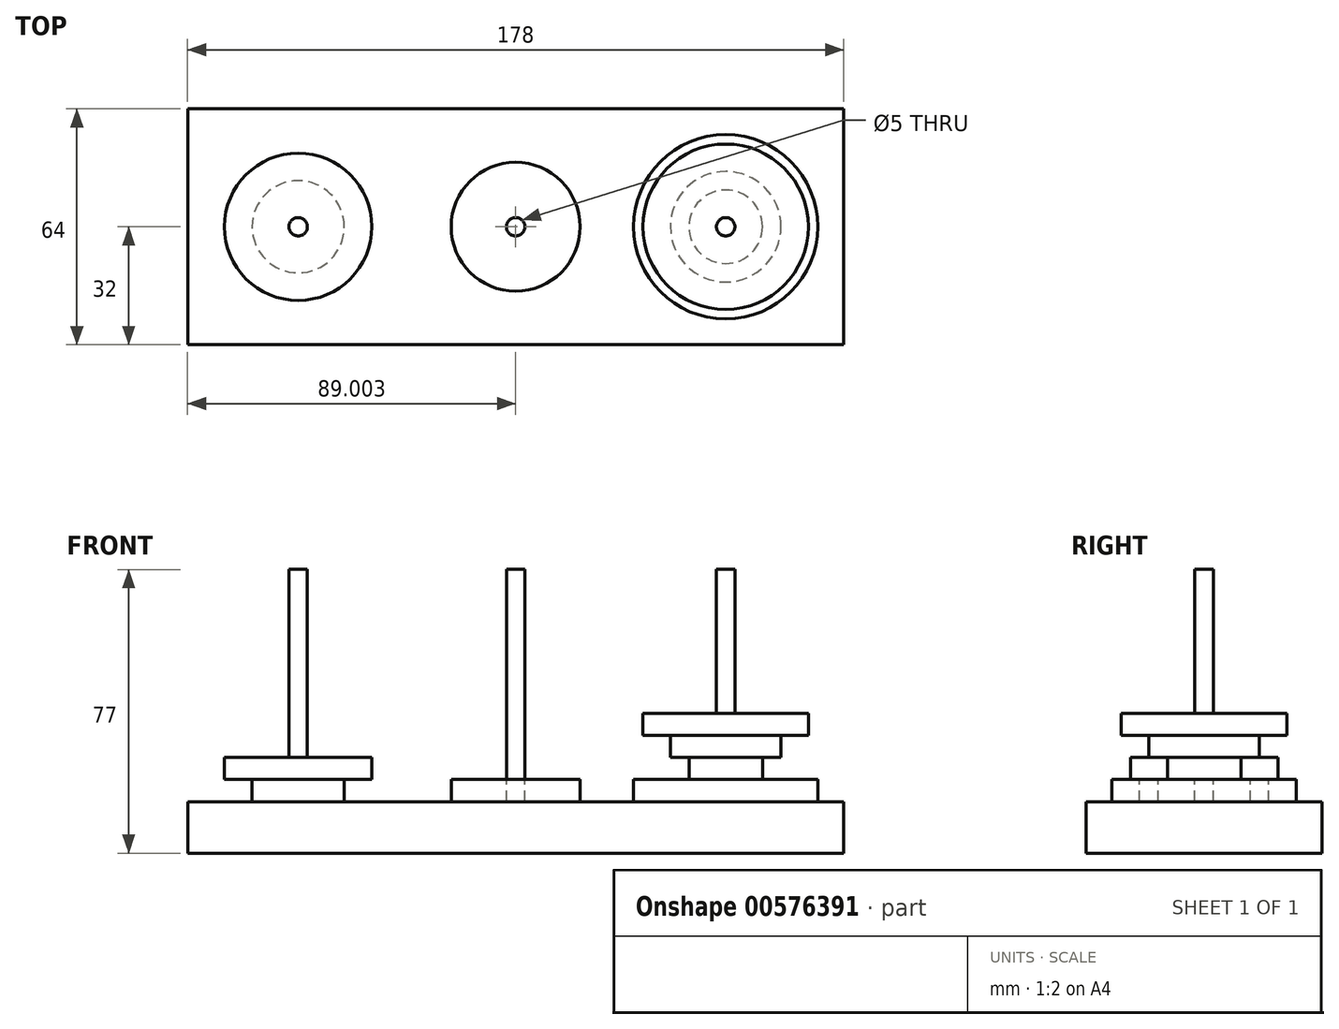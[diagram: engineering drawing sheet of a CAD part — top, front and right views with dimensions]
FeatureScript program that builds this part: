
annotation { "Feature Type Name" : "Feature", "Feature Type Description" : "" }
export const myFeature = defineFeature(function(context is Context, id is Id, definition is map)
    precondition{}
    {
        {
            var Q0;
            Q0=qCreatedBy(makeId("Front.planeOp"),FACE);
            var sketch = newSketch(context, id + "F0", { "sketchPlane" : qUnion([Q0])});
            skLineSegment(sketch, "E0", {"start": v(44.25, 49.56) * mm, "end": v(222.25, 49.56) * mm});
            skLineSegment(sketch, "E1", {"start": v(222.25, 49.56) * mm, "end": v(222.25, 63.56) * mm});
            skLineSegment(sketch, "E2", {"start": v(222.25, 63.56) * mm, "end": v(44.25, 63.56) * mm});
            skLineSegment(sketch, "E3", {"start": v(44.25, 63.56) * mm, "end": v(44.25, 49.56) * mm});
            skSolve(sketch);
        }
        {
            var Q0;
            Q0=makeQuery(id+"F0.imprint","IMPRINT",FACE,{"disambiguationData":[TD([[makeQuery(id+"F0.imprint","IMPRINT",EDGE,{"derivedFrom":sQuery(id+"F0.wireOp",EDGE,"E0")}),1.0]])]});
            extrude(context, id + "F1", {"entities" : qUnion([Q0]), "oppositeDirection" : true, "depth" : 64 * mm, "offsetDistance" : 25 * mm});
        }
        {
            var Q0;
            Q0=makeQuery(id+"F1.opExtrude","CAP_FACE",FACE,{"disambiguationData":[OSD([sQuery(id+"F0.wireOp",EDGE,"E0"),sQuery(id+"F0.wireOp",EDGE,"E1"),sQuery(id+"F0.wireOp",EDGE,"E2"),sQuery(id+"F0.wireOp",EDGE,"E3")])],"isStart":true});
            var sketch = newSketch(context, id + "F2", { "sketchPlane" : qUnion([Q0])});
            skLineSegment(sketch, "E4", {"start": v(44.25, 63.56) * mm, "end": v(103.55, 63.56) * mm});
            skLineSegment(sketch, "E5", {"start": v(103.55, 63.56) * mm, "end": v(162.85, 63.56) * mm});
            skLineSegment(sketch, "E6", {"start": v(162.85, 63.56) * mm, "end": v(222.25, 63.56) * mm});
            skSolve(sketch);
        }
        {
            var Q0;
            Q0=makeQuery(id+"F1.opExtrude","SWEPT_FACE",FACE,{"disambiguationData":[OSD([sQuery(id+"F0.wireOp",EDGE,"E2")])]});
            var sketch = newSketch(context, id + "F3", { "sketchPlane" : qUnion([Q0])});
            skCircle(sketch, "E7", {"center": v(74.25, 32) * mm, "radius": 2.5 * mm});
            skCircle(sketch, "E8", {"center": v(133.25, 32) * mm, "radius": 2.5 * mm});
            skCircle(sketch, "E9", {"center": v(190.25, 32) * mm, "radius": 2.5 * mm});
            skSolve(sketch);
        }
        {
            var Q0;
            Q0=makeQuery(id+"F3.imprint","IMPRINT",FACE,{"disambiguationData":[TD([[makeQuery(id+"F3.imprint","IMPRINT",EDGE,{"derivedFrom":sQuery(id+"F3.wireOp",EDGE,"E7")}),1.0]])]});
            var Q1;
            Q1=makeQuery(id+"F3.imprint","IMPRINT",FACE,{"disambiguationData":[TD([[makeQuery(id+"F3.imprint","IMPRINT",EDGE,{"derivedFrom":sQuery(id+"F3.wireOp",EDGE,"E8")}),1.0]])]});
            var Q2;
            Q2=makeQuery(id+"F3.imprint","IMPRINT",FACE,{"disambiguationData":[TD([[makeQuery(id+"F3.imprint","IMPRINT",EDGE,{"derivedFrom":sQuery(id+"F3.wireOp",EDGE,"E9")}),1.0]])]});
            extrude(context, id + "F4", {"entities" : qUnion([Q0, Q1, Q2]), "operationType" : NewBodyOperationType.ADD, "depth" : 63 * mm, "offsetDistance" : 25 * mm});
        }
        {
            var Q0;
            Q0=makeQuery(id+"F1.opExtrude","SWEPT_FACE",FACE,{"disambiguationData":[OSD([sQuery(id+"F0.wireOp",EDGE,"E2")])]});
            var sketch = newSketch(context, id + "F5", { "sketchPlane" : qUnion([Q0])});
            skLineSegment(sketch, "E10", {"start": v(192.75, 32) * mm, "end": v(215.25, 32) * mm});
            skPoint(sketch, "E10.startSnap0", {"position": v(222.25, 32) * mm});
            skPoint(sketch, "E10.endSnap0", {"position": v(222.25, 32) * mm});
            skSolve(sketch);
        }
        {
            var Q0;
            Q0=sQuery(id+"F5.wireOp",EDGE,"E10");
            extrude(context, id + "F6", {"bodyType" : ToolBodyType.SURFACE, "surfaceEntities" : qUnion([Q0]), "depth" : 6 * mm, "offsetDistance" : 25 * mm});
        }
        {
            var Q0;
            Q0=makeQuery(id+"F6.opExtrude","SWEPT_FACE",FACE,{"disambiguationData":[OSD([sQuery(id+"F5.wireOp",EDGE,"E10")])]});
            var Q1;
            Q1=makeQuery(id+"F4.opExtrude","SWEPT_FACE",FACE,{"disambiguationData":[OSD([sQuery(id+"F3.wireOp",EDGE,"E9")])]});
            revolve(context, id + "F7", {"operationType" : NewBodyOperationType.ADD, "entities" : qUnion([Q0]), "axis" : qUnion([Q1]), "revolveType" : RevolveType.FULL});
        }
        {
            var Q0;
            Q0=makeQuery(id+"F1.opExtrude","SWEPT_FACE",FACE,{"disambiguationData":[OSD([sQuery(id+"F0.wireOp",EDGE,"E2")])]});
            var sketch = newSketch(context, id + "F8", { "sketchPlane" : qUnion([Q0])});
            skLineSegment(sketch, "E11", {"start": v(71.75, 32) * mm, "end": v(61.75, 32) * mm});
            skPoint(sketch, "E11.startSnap0", {"position": v(44.25, 32) * mm});
            skLineSegment(sketch, "E12", {"start": v(130.75, 32) * mm, "end": v(115.75, 32) * mm});
            skSolve(sketch);
        }
        {
            var Q0;
            Q0=sQuery(id+"F8.wireOp",EDGE,"E11");
            var Q1;
            Q1=sQuery(id+"F8.wireOp",EDGE,"E12");
            extrude(context, id + "F9", {"bodyType" : ToolBodyType.SURFACE, "surfaceEntities" : qUnion([Q0, Q1]), "depth" : 6 * mm, "offsetDistance" : 25 * mm});
        }
        {
            var Q0;
            Q0=makeQuery(id+"F9.opExtrude","SWEPT_FACE",FACE,{"disambiguationData":[OSD([sQuery(id+"F8.wireOp",EDGE,"E11")])]});
            var Q1;
            Q1=makeQuery(id+"F4.opExtrude","SWEPT_FACE",FACE,{"disambiguationData":[OSD([sQuery(id+"F3.wireOp",EDGE,"E7")])]});
            revolve(context, id + "F10", {"operationType" : NewBodyOperationType.ADD, "entities" : qUnion([Q0]), "axis" : qUnion([Q1]), "revolveType" : RevolveType.FULL});
        }
        {
            var Q0;
            Q0=makeQuery(id+"F9.opExtrude","SWEPT_FACE",FACE,{"disambiguationData":[OSD([sQuery(id+"F8.wireOp",EDGE,"E12")])]});
            var Q1;
            Q1=makeQuery(id+"F4.opExtrude","SWEPT_FACE",FACE,{"disambiguationData":[OSD([sQuery(id+"F3.wireOp",EDGE,"E8")])]});
            revolve(context, id + "F11", {"entities" : qUnion([Q0]), "axis" : qUnion([Q1]), "revolveType" : RevolveType.FULL});
        }
        {
            var Q0;
            {var subQ0=sQuery(id+"F5.wireOp",EDGE,"E10");Q0=makeQuery(id+"F7.opRevolve","SWEPT_FACE",FACE,{"disambiguationData":[OSD([subQ0]),TDD([makeQuery(id+"F6.opExtrude","CAP_EDGE",EDGE,{"disambiguationData":[OSD([subQ0])],"isStart":false})])]});}
            var sketch = newSketch(context, id + "F12", { "sketchPlane" : qUnion([Q0])});
            skLineSegment(sketch, "E13", {"start": v(187.92, 32.89) * mm, "end": v(181.36, 36.53) * mm});
            skSolve(sketch);
        }
        {
            var Q0;
            Q0=sQuery(id+"F12.wireOp",EDGE,"E13");
            extrude(context, id + "F13", {"bodyType" : ToolBodyType.SURFACE, "surfaceEntities" : qUnion([Q0]), "depth" : 6 * mm, "offsetDistance" : 25 * mm});
        }
        {
            var Q0;
            Q0=makeQuery(id+"F13.opExtrude","SWEPT_FACE",FACE,{"disambiguationData":[OSD([sQuery(id+"F12.wireOp",EDGE,"E13")])]});
            var Q1;
            Q1=makeQuery(id+"F4.opExtrude","SWEPT_FACE",FACE,{"disambiguationData":[OSD([sQuery(id+"F3.wireOp",EDGE,"E9")])]});
            revolve(context, id + "F14", {"operationType" : NewBodyOperationType.ADD, "entities" : qUnion([Q0]), "axis" : qUnion([Q1]), "revolveType" : RevolveType.FULL});
        }
        {
            var Q0;
            {var subQ0=sQuery(id+"F8.wireOp",EDGE,"E11");Q0=makeQuery(id+"F10.opRevolve","SWEPT_FACE",FACE,{"disambiguationData":[OSD([subQ0]),TDD([makeQuery(id+"F9.opExtrude","CAP_EDGE",EDGE,{"disambiguationData":[OSD([subQ0])],"isStart":false})])]});}
            var sketch = newSketch(context, id + "F15", { "sketchPlane" : qUnion([Q0])});
            skLineSegment(sketch, "E14", {"start": v(76.75, 31.97) * mm, "end": v(94.25, 31.97) * mm});
            skSolve(sketch);
        }
        {
            var Q0;
            Q0=sQuery(id+"F15.wireOp",EDGE,"E14");
            extrude(context, id + "F16", {"bodyType" : ToolBodyType.SURFACE, "surfaceEntities" : qUnion([Q0]), "depth" : 6 * mm, "offsetDistance" : 25 * mm});
        }
        {
            var Q0;
            Q0=makeQuery(id+"F16.opExtrude","SWEPT_FACE",FACE,{"disambiguationData":[OSD([sQuery(id+"F15.wireOp",EDGE,"E14")])]});
            var Q1;
            Q1=makeQuery(id+"F4.opExtrude","SWEPT_FACE",FACE,{"disambiguationData":[OSD([sQuery(id+"F3.wireOp",EDGE,"E7")])]});
            revolve(context, id + "F17", {"operationType" : NewBodyOperationType.ADD, "entities" : qUnion([Q0]), "axis" : qUnion([Q1]), "revolveType" : RevolveType.FULL});
        }
        {
            var Q0;
            {var subQ0=sQuery(id+"F12.wireOp",EDGE,"E13");Q0=makeQuery(id+"F14.opRevolve","SWEPT_FACE",FACE,{"disambiguationData":[OSD([subQ0]),TDD([makeQuery(id+"F13.opExtrude","CAP_EDGE",EDGE,{"disambiguationData":[OSD([subQ0])],"isStart":false})])]});}
            var sketch = newSketch(context, id + "F18", { "sketchPlane" : qUnion([Q0])});
            skLineSegment(sketch, "E15", {"start": v(192.74, 32.23) * mm, "end": v(205.24, 32.23) * mm});
            skSolve(sketch);
        }
        {
            var Q0;
            Q0=sQuery(id+"F18.wireOp",EDGE,"E15");
            extrude(context, id + "F19", {"bodyType" : ToolBodyType.SURFACE, "surfaceEntities" : qUnion([Q0]), "depth" : 6 * mm, "offsetDistance" : 25 * mm});
        }
        {
            var Q0;
            Q0=makeQuery(id+"F19.opExtrude","SWEPT_FACE",FACE,{"disambiguationData":[OSD([sQuery(id+"F18.wireOp",EDGE,"E15")])]});
            var Q1;
            Q1=makeQuery(id+"F4.opExtrude","SWEPT_FACE",FACE,{"disambiguationData":[OSD([sQuery(id+"F3.wireOp",EDGE,"E9")])]});
            revolve(context, id + "F20", {"operationType" : NewBodyOperationType.ADD, "entities" : qUnion([Q0]), "axis" : qUnion([Q1]), "revolveType" : RevolveType.FULL});
        }
        {
            var Q0;
            {var subQ0=sQuery(id+"F18.wireOp",EDGE,"E15");Q0=makeQuery(id+"F20.opRevolve","SWEPT_FACE",FACE,{"disambiguationData":[OSD([subQ0]),TDD([makeQuery(id+"F19.opExtrude","CAP_EDGE",EDGE,{"disambiguationData":[OSD([subQ0])],"isStart":false})])]});}
            var sketch = newSketch(context, id + "F21", { "sketchPlane" : qUnion([Q0])});
            skLineSegment(sketch, "E16", {"start": v(187.82, 32.6) * mm, "end": v(167.82, 32.6) * mm});
            skSolve(sketch);
        }
        {
            var Q0;
            Q0=sQuery(id+"F21.wireOp",EDGE,"E16");
            extrude(context, id + "F22", {"bodyType" : ToolBodyType.SURFACE, "surfaceEntities" : qUnion([Q0]), "depth" : 6 * mm, "offsetDistance" : 25 * mm});
        }
        {
            var Q0;
            Q0=makeQuery(id+"F22.opExtrude","SWEPT_FACE",FACE,{"disambiguationData":[OSD([sQuery(id+"F21.wireOp",EDGE,"E16")])]});
            var Q1;
            Q1=makeQuery(id+"F4.opExtrude","SWEPT_FACE",FACE,{"disambiguationData":[OSD([sQuery(id+"F3.wireOp",EDGE,"E9")])]});
            revolve(context, id + "F23", {"operationType" : NewBodyOperationType.ADD, "entities" : qUnion([Q0]), "axis" : qUnion([Q1]), "revolveType" : RevolveType.FULL});
        }
    });
